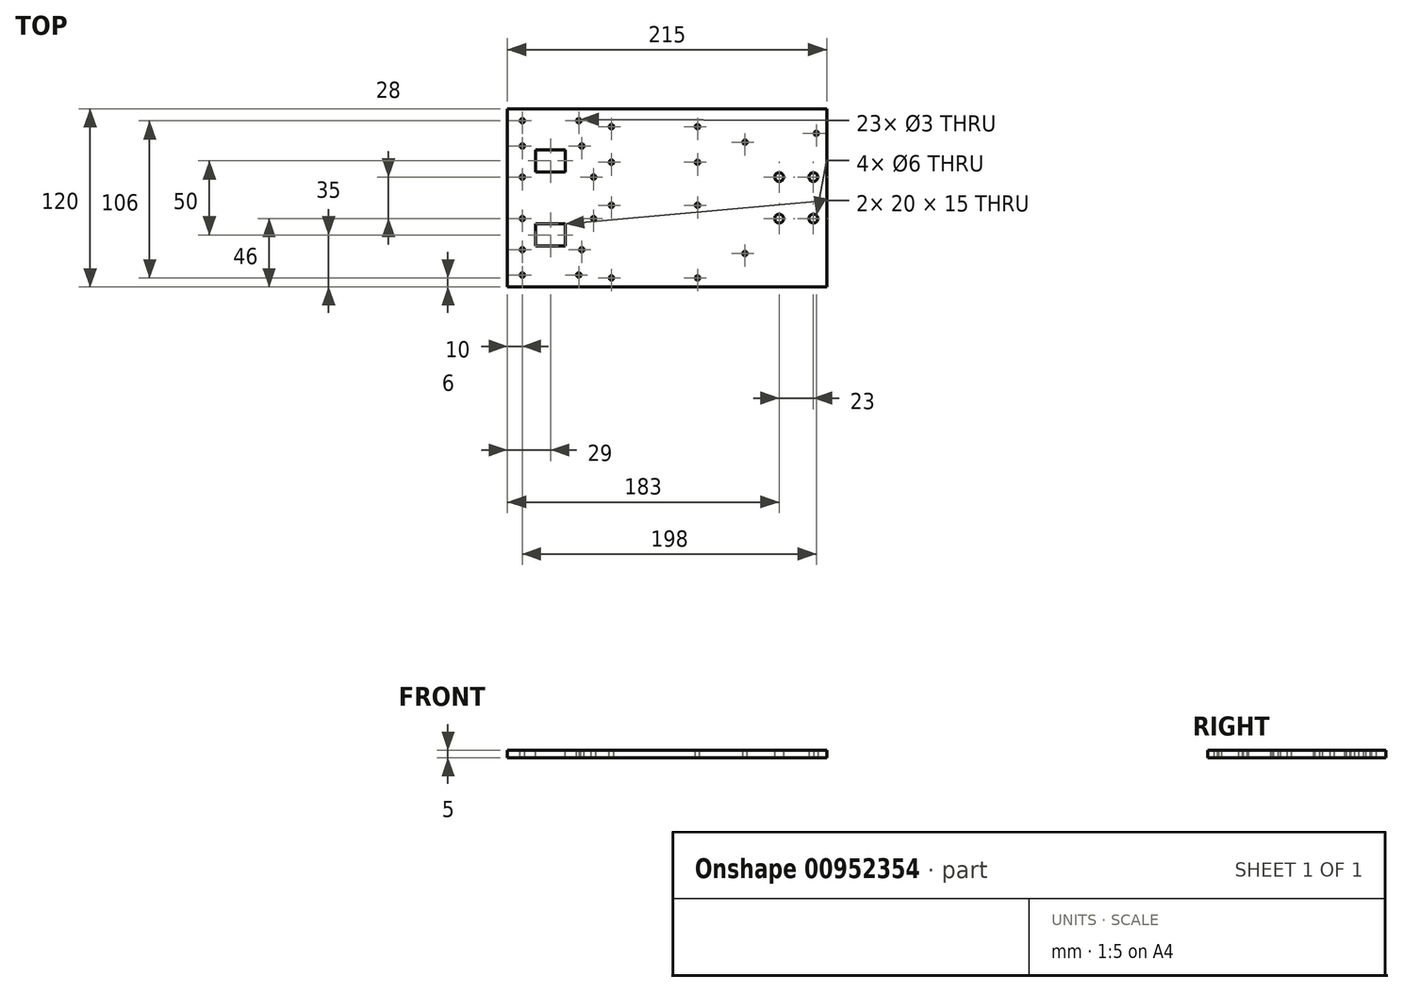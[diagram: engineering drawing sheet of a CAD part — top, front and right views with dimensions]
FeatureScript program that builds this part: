
annotation { "Feature Type Name" : "Feature", "Feature Type Description" : "" }
export const myFeature = defineFeature(function(context is Context, id is Id, definition is map)
    precondition{}
    {
        {
            var Q0;
            Q0=qCreatedBy(makeId("Top.planeOp"),FACE);
            var sketch = newSketch(context, id + "F0", { "sketchPlane" : qUnion([Q0])});
            skLineSegment(sketch, "E0.bottom", {"start": v(107.5, 60) * mm, "end": v(-107.5, 60) * mm});
            skLineSegment(sketch, "E0.top", {"start": v(107.5, -60) * mm, "end": v(-107.5, -60) * mm});
            skLineSegment(sketch, "E0.left", {"start": v(107.5, 60) * mm, "end": v(107.5, -60) * mm});
            skLineSegment(sketch, "E0.right", {"start": v(-107.5, 60) * mm, "end": v(-107.5, -60) * mm});
            skPoint(sketch, "E0.middle", {"position": v(0, 0) * mm});
            skSolve(sketch);
        }
        {
            var Q0;
            Q0 = qSketchRegion(id + "F0", true);
            extrude(context, id + "F1", {"entities" : qUnion([Q0]), "depth" : 5 * mm, "offsetDistance" : 25 * mm});
        }
        {
            var Q0;
            Q0=makeQuery(id+"F1.opExtrude","CAP_FACE",FACE,{"disambiguationData":[OSD([sQuery(id+"F0.wireOp",EDGE,"E0.bottom"),sQuery(id+"F0.wireOp",EDGE,"E0.top"),sQuery(id+"F0.wireOp",EDGE,"E0.left"),sQuery(id+"F0.wireOp",EDGE,"E0.right"),sQuery(id+"F0.wireOp",EDGE,"IeUhD8lu-sktF-GMrU-8Srv-e3DhNs2p6vg7.bottom"),sQuery(id+"F0.wireOp",EDGE,"IeUhD8lu-sktF-GMrU-8Srv-e3DhNs2p6vg7.top"),sQuery(id+"F0.wireOp",EDGE,"IeUhD8lu-sktF-GMrU-8Srv-e3DhNs2p6vg7.left"),sQuery(id+"F0.wireOp",EDGE,"IeUhD8lu-sktF-GMrU-8Srv-e3DhNs2p6vg7.right")])],"isStart":false});
            var sketch = newSketch(context, id + "F2", { "sketchPlane" : qUnion([Q0])});
            skCircle(sketch, "E1", {"center": v(-97.5, 52) * mm, "radius": 1.5 * mm});
            skCircle(sketch, "E2", {"center": v(-59.5, 52) * mm, "radius": 1.5 * mm});
            skCircle(sketch, "E3.MirrorC", {"center": v(-97.5, -52) * mm, "radius": 1.5 * mm});
            skCircle(sketch, "E4.MirrorC", {"center": v(-59.5, -52) * mm, "radius": 1.5 * mm});
            skLineSegment(sketch, "E5", {"start": v(-97.5, -52) * mm, "end": v(-59.5, -52) * mm, "construction": true});
            skPoint(sketch, "E6", {"position": v(-78.5, -52) * mm});
            skLineSegment(sketch, "E7.bottom", {"start": v(-68.5, 17.5) * mm, "end": v(-88.5, 17.5) * mm});
            skLineSegment(sketch, "E7.top", {"start": v(-68.5, 32.5) * mm, "end": v(-88.5, 32.5) * mm});
            skLineSegment(sketch, "E7.left", {"start": v(-68.5, 17.5) * mm, "end": v(-68.5, 32.5) * mm});
            skLineSegment(sketch, "E7.right", {"start": v(-88.5, 17.5) * mm, "end": v(-88.5, 32.5) * mm});
            skPoint(sketch, "E7.middle", {"position": v(-78.5, 25) * mm});
            skLineSegment(sketch, "E8.MirrorCS", {"start": v(-68.5, -32.5) * mm, "end": v(-88.5, -32.5) * mm});
            skLineSegment(sketch, "E9.MirrorCS", {"start": v(-88.5, -17.5) * mm, "end": v(-88.5, -32.5) * mm});
            skLineSegment(sketch, "E10.MirrorCS", {"start": v(-68.5, -17.5) * mm, "end": v(-68.5, -32.5) * mm});
            skPoint(sketch, "E11.MirrorP", {"position": v(-78.5, -25) * mm});
            skLineSegment(sketch, "E12.MirrorCS", {"start": v(-68.5, -17.5) * mm, "end": v(-88.5, -17.5) * mm});
            skSolve(sketch);
        }
        {
            var Q0;
            Q0 = qSketchRegion(id + "F2", true);
            extrude(context, id + "F3", {"entities" : qUnion([Q0]), "operationType" : NewBodyOperationType.REMOVE, "oppositeDirection" : true, "depth" : 25 * mm, "offsetDistance" : 25 * mm});
        }
        {
            var Q0;
            Q0=makeQuery(id+"F1.opExtrude","CAP_FACE",FACE,{"disambiguationData":[OSD([sQuery(id+"F0.wireOp",EDGE,"E0.bottom"),sQuery(id+"F0.wireOp",EDGE,"E0.top"),sQuery(id+"F0.wireOp",EDGE,"E0.left"),sQuery(id+"F0.wireOp",EDGE,"E0.right")])],"isStart":false});
            var sketch = newSketch(context, id + "F4", { "sketchPlane" : qUnion([Q0])});
            skCircle(sketch, "E13", {"center": v(-37.5, -54) * mm, "radius": 1.5 * mm});
            skCircle(sketch, "E14.0.1.0", {"center": v(-37.5, -5) * mm, "radius": 1.5 * mm});
            skCircle(sketch, "E14.1.0.0", {"center": v(20.5, -54) * mm, "radius": 1.5 * mm});
            skCircle(sketch, "E14.1.1.0", {"center": v(20.5, -5) * mm, "radius": 1.5 * mm});
            skLineSegment(sketch, "E14.direction1", {"start": v(-37.5, -54) * mm, "end": v(20.5, -54) * mm, "construction": true});
            skLineSegment(sketch, "E14.direction2", {"start": v(-37.5, -54) * mm, "end": v(-37.5, -5) * mm, "construction": true});
            skSolve(sketch);
        }
        {
            var Q0;
            Q0 = qSketchRegion(id + "F4", true);
            extrude(context, id + "F5", {"entities" : qUnion([Q0]), "operationType" : NewBodyOperationType.REMOVE, "endBound" : BoundingType.THROUGH_ALL, "oppositeDirection" : true, "depth" : 25 * mm, "offsetDistance" : 25 * mm});
        }
        {
            var Q0;
            Q0=makeQuery(id+"F1.opExtrude","CAP_FACE",FACE,{"disambiguationData":[OSD([sQuery(id+"F0.wireOp",EDGE,"E0.bottom"),sQuery(id+"F0.wireOp",EDGE,"E0.top"),sQuery(id+"F0.wireOp",EDGE,"E0.left"),sQuery(id+"F0.wireOp",EDGE,"E0.right")])],"isStart":true});
            var sketch = newSketch(context, id + "F6", { "sketchPlane" : qUnion([Q0])});
            skCircle(sketch, "E15", {"center": v(98.5, -14) * mm, "radius": 3 * mm});
            skCircle(sketch, "E16.0.1.0", {"center": v(98.5, 14) * mm, "radius": 3 * mm});
            skCircle(sketch, "E16.1.0.0", {"center": v(75.5, -14) * mm, "radius": 3 * mm});
            skCircle(sketch, "E16.1.1.0", {"center": v(75.5, 14) * mm, "radius": 3 * mm});
            skLineSegment(sketch, "E16.direction1", {"start": v(98.5, -14) * mm, "end": v(75.5, -14) * mm, "construction": true});
            skLineSegment(sketch, "E16.direction2", {"start": v(98.5, -14) * mm, "end": v(98.5, 14) * mm, "construction": true});
            skSolve(sketch);
        }
        {
            var Q0;
            Q0 = qSketchRegion(id + "F6", true);
            extrude(context, id + "F7", {"entities" : qUnion([Q0]), "operationType" : NewBodyOperationType.REMOVE, "endBound" : BoundingType.THROUGH_ALL, "oppositeDirection" : true, "depth" : 25 * mm, "offsetDistance" : 25 * mm});
        }
        {
            var Q0;
            Q0=makeQuery(id+"F1.opExtrude","CAP_FACE",FACE,{"disambiguationData":[OSD([sQuery(id+"F0.wireOp",EDGE,"E0.bottom"),sQuery(id+"F0.wireOp",EDGE,"E0.top"),sQuery(id+"F0.wireOp",EDGE,"E0.left"),sQuery(id+"F0.wireOp",EDGE,"E0.right")])],"isStart":false});
            var sketch = newSketch(context, id + "F8", { "sketchPlane" : qUnion([Q0])});
            skCircle(sketch, "E17", {"center": v(-37.5, 48) * mm, "radius": 1.5 * mm});
            skCircle(sketch, "E18.0.1.0", {"center": v(-37.5, 24) * mm, "radius": 1.5 * mm});
            skCircle(sketch, "E18.1.0.0", {"center": v(20.5, 48) * mm, "radius": 1.5 * mm});
            skCircle(sketch, "E18.1.1.0", {"center": v(20.5, 24) * mm, "radius": 1.5 * mm});
            skLineSegment(sketch, "E18.direction1", {"start": v(-37.5, 48) * mm, "end": v(20.5, 48) * mm, "construction": true});
            skLineSegment(sketch, "E18.direction2", {"start": v(-37.5, 48) * mm, "end": v(-37.5, 24) * mm, "construction": true});
            skSolve(sketch);
        }
        {
            var Q0;
            Q0 = qSketchRegion(id + "F8", true);
            extrude(context, id + "F9", {"entities" : qUnion([Q0]), "operationType" : NewBodyOperationType.REMOVE, "endBound" : BoundingType.THROUGH_ALL, "oppositeDirection" : true, "depth" : 25 * mm, "offsetDistance" : 25 * mm});
        }
        {
            var Q0;
            Q0=makeQuery(id+"F1.opExtrude","CAP_FACE",FACE,{"disambiguationData":[OSD([sQuery(id+"F0.wireOp",EDGE,"E0.bottom"),sQuery(id+"F0.wireOp",EDGE,"E0.top"),sQuery(id+"F0.wireOp",EDGE,"E0.left"),sQuery(id+"F0.wireOp",EDGE,"E0.right")])],"isStart":false});
            var sketch = newSketch(context, id + "F10", { "sketchPlane" : qUnion([Q0])});
            skCircle(sketch, "E19", {"center": v(-97.5, 14) * mm, "radius": 1.5 * mm});
            skCircle(sketch, "E20.0.1.0", {"center": v(-97.5, -14) * mm, "radius": 1.5 * mm});
            skCircle(sketch, "E20.1.0.0", {"center": v(-49.5, 14) * mm, "radius": 1.5 * mm});
            skCircle(sketch, "E20.1.1.0", {"center": v(-49.5, -14) * mm, "radius": 1.5 * mm});
            skLineSegment(sketch, "E20.direction1", {"start": v(-97.5, 14) * mm, "end": v(-49.5, 14) * mm, "construction": true});
            skLineSegment(sketch, "E20.direction2", {"start": v(-97.5, 14) * mm, "end": v(-97.5, -14) * mm, "construction": true});
            skPoint(sketch, "E21", {"position": v(-97.5, 0) * mm});
            skSolve(sketch);
        }
        {
            var Q0;
            Q0 = qSketchRegion(id + "F10", true);
            extrude(context, id + "F11", {"entities" : qUnion([Q0]), "operationType" : NewBodyOperationType.REMOVE, "endBound" : BoundingType.THROUGH_ALL, "oppositeDirection" : true, "depth" : 25 * mm, "offsetDistance" : 25 * mm});
        }
        {
            var Q0;
            Q0=makeQuery(id+"F1.opExtrude","CAP_FACE",FACE,{"disambiguationData":[OSD([sQuery(id+"F0.wireOp",EDGE,"E0.bottom"),sQuery(id+"F0.wireOp",EDGE,"E0.top"),sQuery(id+"F0.wireOp",EDGE,"E0.left"),sQuery(id+"F0.wireOp",EDGE,"E0.right")])],"isStart":false});
            var sketch = newSketch(context, id + "F12", { "sketchPlane" : qUnion([Q0])});
            skCircle(sketch, "E22", {"center": v(-57.5, 35) * mm, "radius": 1.5 * mm});
            skCircle(sketch, "E23", {"center": v(-57.5, -35) * mm, "radius": 1.5 * mm});
            skLineSegment(sketch, "E24", {"start": v(-57.5, 35) * mm, "end": v(-57.5, -35) * mm, "construction": true});
            skPoint(sketch, "E25", {"position": v(-57.5, 0) * mm});
            skCircle(sketch, "E26.1.0.0", {"center": v(-97.5, 35) * mm, "radius": 1.5 * mm});
            skCircle(sketch, "E26.1.0.1", {"center": v(-97.5, -35) * mm, "radius": 1.5 * mm});
            skLineSegment(sketch, "E26.direction1", {"start": v(-57.5, 35) * mm, "end": v(-97.5, 35) * mm, "construction": true});
            skSolve(sketch);
        }
        {
            var Q0;
            Q0 = qSketchRegion(id + "F12", true);
            extrude(context, id + "F13", {"entities" : qUnion([Q0]), "operationType" : NewBodyOperationType.REMOVE, "endBound" : BoundingType.THROUGH_ALL, "oppositeDirection" : true, "depth" : 25 * mm, "offsetDistance" : 25 * mm});
        }
        {
            var Q0;
            Q0=makeQuery(id+"F1.opExtrude","CAP_FACE",FACE,{"disambiguationData":[OSD([sQuery(id+"F0.wireOp",EDGE,"E0.bottom"),sQuery(id+"F0.wireOp",EDGE,"E0.top"),sQuery(id+"F0.wireOp",EDGE,"E0.left"),sQuery(id+"F0.wireOp",EDGE,"E0.right")])],"isStart":false});
            var sketch = newSketch(context, id + "F14", { "sketchPlane" : qUnion([Q0])});
            skCircle(sketch, "E27", {"center": v(52.5, 37.5) * mm, "radius": 1.5 * mm});
            skCircle(sketch, "E28", {"center": v(100.5, 43.5) * mm, "radius": 1.5 * mm});
            skCircle(sketch, "E29", {"center": v(52.5, -37.5) * mm, "radius": 1.5 * mm});
            skLineSegment(sketch, "E30", {"start": v(52.5, 37.5) * mm, "end": v(52.5, -37.5) * mm, "construction": true});
            skPoint(sketch, "E31", {"position": v(52.5, 0) * mm});
            skSolve(sketch);
        }
        {
            var Q0;
            Q0 = qSketchRegion(id + "F14", true);
            extrude(context, id + "F15", {"entities" : qUnion([Q0]), "operationType" : NewBodyOperationType.REMOVE, "endBound" : BoundingType.THROUGH_ALL, "oppositeDirection" : true, "depth" : 25 * mm, "offsetDistance" : 25 * mm});
        }
    });
